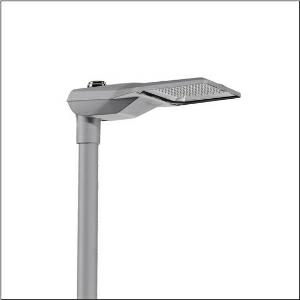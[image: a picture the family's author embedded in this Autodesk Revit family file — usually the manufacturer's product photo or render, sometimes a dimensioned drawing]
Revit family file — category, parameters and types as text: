
# Revit family: streetlight_sl_21_midi___st1_0a_5xe7d57n08mb_4ce1
name_source: partatom
category: Lighting Fixtures
units: mm (PartAtom-declared; Revit-internal decimal feet)

## family parameters
Cut with Voids When Loaded = No
Host = Face
Light Source = No
Part Type = Normal
Room Calculation Point = No
Round Connector Dimension = Use Diameter
Shared = No

## types (1)
- --- (1 x LED, 15800 lm, 137 W, 3000K)
    Apparent Load = 137 VA
    CIE Flux Codes = 37 72 97 100 100
    Color Rendering = 80
    Color Temperature = 3000K
    Default Elevation = 1800 mm
    Description = Streetlight SL 21 midi, mast luminaire, primary light control with lens, of PMMA, primary optical cover: cover, of toughened safety glass, transparent, light distribution: ST1.0a, light emission: direct distribution, primary light characteristic: asymmetric, installation type: side-entry, LED, 3G 2.5mm², High Power LED, rated luminous flux: 15.800lm, luminous efficacy: 115lm/W, light colour: 830, colour temperature: 3000K, control gear: NEMA (7pin), control: overheat protection, pre-setting: linear dimming characteristic, constant luminous flux control, time-dependent luminous flux control, flexible luminous flux parameterisation, mains connection: 220..240V, AC, 50/60Hz, connection cable pre-assembled, cable length: 12,5m, wiring characteristics: H05VV-F, start of lifetime: 137W, end of service life: 144W, reduction: 61W, luminaire housing, of diecast aluminium (EN AC-44300), powder-coated, SITECO metallic grey (DB 702S), corrosivity category C5 high according to DIN EN ISO 12944, multi-level sealing system, sealing non-destructively replaceable, inclination adjustable: 0°, 5°, 10°, 15°, length: 644mm, width: 335mm, height: 110mm, spigot size: 42mm (side-entry), mounting height: 4..8m, protection rating (complete): IP66, insulation class (complete): insulation class I (protective earthing), certification: CE, ENEC, ENEC+, VDE, impact resistance: IK10, permissible operating ambient temperature for outdoor applications: -40..+50°C, standard-compliant lighting for roads and squares, packaging unit: 1 piece

Light Distribution: ST1.0a
    Height = 111 mm
    Lamp = 1 x LED
    Lamp Light Flux = 15800 lm
    Lamp Power = 137 W
    Lamp count = 1
    Length = 644 mm
    Luminous efficacy = 115 lm/W
    Manufacturer = Siteco
    ModVariant = No
    Model = 5XE7D57N08MB
    Number of Poles = 1
    OnlyDefault = Yes
    Power Factor = 1
    Product Name = Streetlight SL 21 midi | ST1.0a
    Product group = mast luminaire | pylon top
    ProductGroupID = 6100
    Protection Class = Protection class I
    Protection Degree = IP 66
    RLX_Detail_Level = 1
    RLX_Emergency_Light_Flux = 0 lm
    RLX_Emergency_Type = 0
    RLX_Emergency_Type_DB = No
    RlxData = <blob elided: 26541 chars, md5=b6045bfe>
    Socket = socket
    Standby Power = 0 W
    System Light Flux = 15800 lm
    System Power = 137 W
    Type Comments = factory setting: luminous flux: 100 % | dim-lin: 254 | 700 mA
    Type Image = l_1294377.jpg
    URL = http://relux.com
    VarID = @adj_135427
    Voltage = 0 V
    Weight = 0.00 kg
    Width = 336 mm

## geometry (parser evidence)
native form markers: Blend x4, Sweep x10
no freeform markers — native parametric forms only
